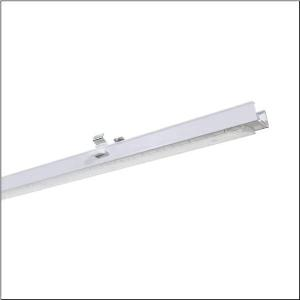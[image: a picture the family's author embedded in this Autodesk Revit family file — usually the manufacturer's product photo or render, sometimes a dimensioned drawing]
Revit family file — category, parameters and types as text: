
# Revit family: trunking_flex_31_51re12mb5cb
name_source: partatom
category: Lighting Fixtures
units: mm (PartAtom-declared; Revit-internal decimal feet)

## family parameters
Cut with Voids When Loaded = No
Host = Face
Light Source = No
Part Type = Normal
Room Calculation Point = No
Round Connector Dimension = Use Diameter
Shared = No

## types (1)
- --- (1 x LED, 11500 lm, 66 W, 5000K)
    Apparent Load = 66 VA
    CIE Flux Codes = 65 91 98 99 100
    Color Rendering = 80
    Color Temperature = 5000K
    Default Elevation = 1800 mm
    Description = Trunking Flex 31, luminaire insert, of extruded aluminium section, coated, traffic white (RAL 9016), length: 1.472mm, width: 91mm, height: 53mm, LED rated luminous flux: 11.500lm, light colour: 850, control gear: ON/OFF Multilumen, with system connector: socket, mains connection: 220..240V, AC, 50/60Hz, rated input power: 66W, luminous flux adjustable on luminaire in eight steps (3450/4380/5800/6700/8350/9200/10500/11500lm ), connected load according to luminous flux setting (19/24/32/37/47/52/60/66W), primary light control with lens, of plastic, primary optical cover: cover, of PMMA, light emission: direct distribution, protection rating (complete): IP20, insulation class (complete): insulation class I (protective earthing), certification: CE, UKCA, impact resistance: IK02, permissible ambient temperature for indoor applications: -20..+40°C, packaging unit: 1 piece
    Height = 58 mm
    Lamp = 1 x LED
    Lamp Light Flux = 11500 lm
    Lamp Power = 66 W
    Lamp count = 1
    Length = 1472 mm
    Luminous efficacy = 174 lm/W
    Manufacturer = Siteco
    ModVariant = No
    Model = 51RE12MB5CB
    Mounting Place = Ceiling
    Mounting Type = Pendant
    Number of Poles = 1
    OnlyDefault = Yes
    Power Factor = 1
    Product Name = Trunking Flex 31
    Product group = luminaire insert
    ProductGroupID = 901
    Protection Class = Protection class I
    Protection Degree = IP 20
    RLX_Detail_Level = 1
    RLX_Emergency_Light_Flux = 0 lm
    RLX_Emergency_Type = 0
    RLX_Emergency_Type_DB = No
    RlxData = <blob elided: 20993 chars, md5=e364cca3>
    Socket = socket
    Standby Power = 0 W
    System Light Flux = 11500 lm
    System Power = 66 W
    Type Comments = factory setting: luminous flux: 100 % | (ON | ON | ON)
    Type Image = l_1266702.jpg
    URL = http://relux.com
    VarID = @adj_001233
    Voltage = 0 V
    Weight = 0.00 kg
    Width = 65 mm

## geometry (parser evidence)
native form markers: Blend x4, Sweep x9
no freeform markers — native parametric forms only
